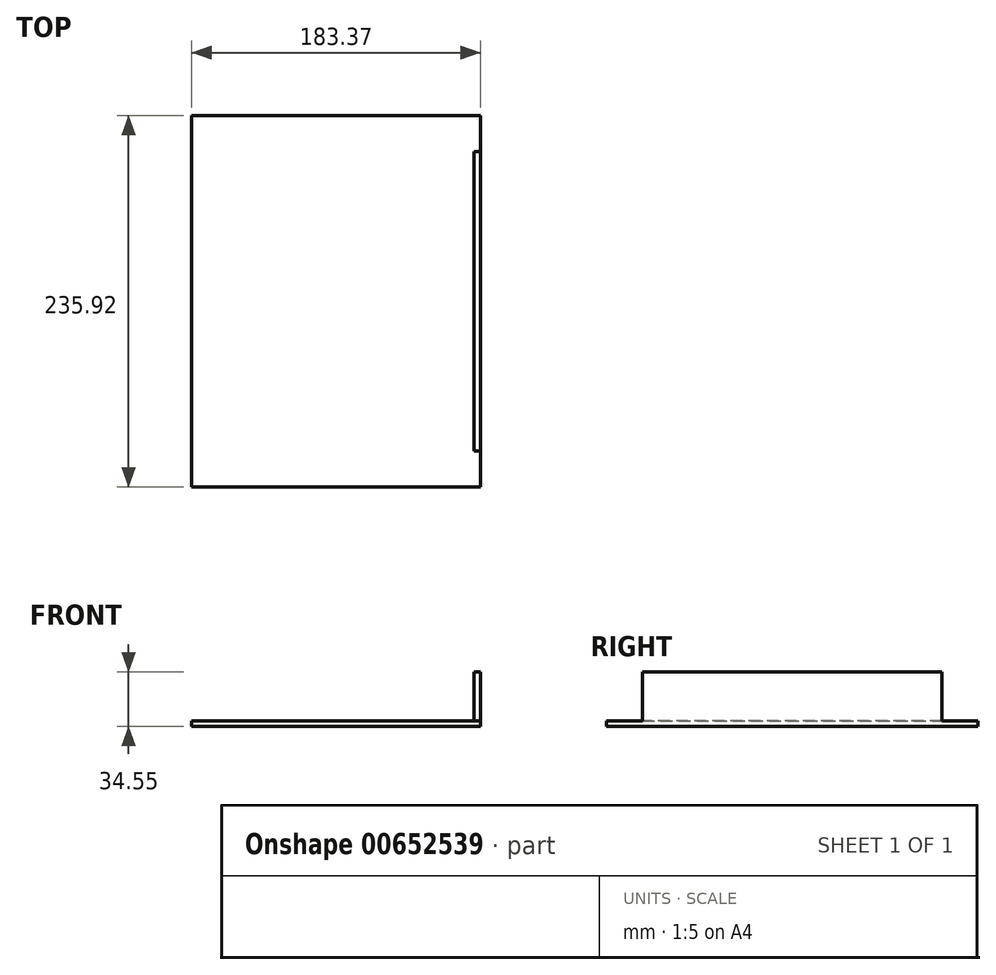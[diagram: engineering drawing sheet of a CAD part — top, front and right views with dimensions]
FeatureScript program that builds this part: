
annotation { "Feature Type Name" : "Feature", "Feature Type Description" : "" }
export const myFeature = defineFeature(function(context is Context, id is Id, definition is map)
    precondition{}
    {
        {
            var Q0;
            Q0=qCreatedBy(makeId("Top.planeOp"),FACE);
            var sketch = newSketch(context, id + "F0", { "sketchPlane" : qUnion([Q0])});
            skLineSegment(sketch, "E0.bottom", {"start": v(-86.94, 111.9) * mm, "end": v(96.43, 111.9) * mm});
            skLineSegment(sketch, "E0.top", {"start": v(-86.94, -124.02) * mm, "end": v(96.43, -124.02) * mm});
            skLineSegment(sketch, "E0.left", {"start": v(-86.94, 111.9) * mm, "end": v(-86.94, -124.02) * mm});
            skLineSegment(sketch, "E0.right", {"start": v(96.43, 111.9) * mm, "end": v(96.43, -124.02) * mm});
            skSolve(sketch);
        }
        {
            var Q0;
            Q0=makeQuery(id+"F0.imprint","IMPRINT",FACE,{"disambiguationData":[TD([[makeQuery(id+"F0.imprint","IMPRINT",EDGE,{"derivedFrom":sQuery(id+"F0.wireOp",EDGE,"E0.bottom")}),-1.0]])]});
            extrude(context, id + "F1", {"entities" : qUnion([Q0]), "oppositeDirection" : true, "depth" : 3.56 * mm, "offsetDistance" : 25.4 * mm});
        }
        {
            var Q0;
            Q0=makeQuery(id+"F1.opExtrude","CAP_FACE",FACE,{"disambiguationData":[OSD([sQuery(id+"F0.wireOp",EDGE,"E0.bottom"),sQuery(id+"F0.wireOp",EDGE,"E0.top"),sQuery(id+"F0.wireOp",EDGE,"E0.left"),sQuery(id+"F0.wireOp",EDGE,"E0.right")])],"isStart":true});
            var sketch = newSketch(context, id + "F2", { "sketchPlane" : qUnion([Q0])});
            skLineSegment(sketch, "E1.bottom", {"start": v(92.31, -101.03) * mm, "end": v(96.43, -101.03) * mm});
            skLineSegment(sketch, "E1.top", {"start": v(92.31, 89) * mm, "end": v(96.43, 89) * mm});
            skLineSegment(sketch, "E1.left", {"start": v(92.31, -101.03) * mm, "end": v(92.31, 89) * mm});
            skLineSegment(sketch, "E1.right", {"start": v(96.43, -101.03) * mm, "end": v(96.43, 89) * mm});
            skSolve(sketch);
        }
        {
            var Q0;
            Q0=makeQuery(id+"F2.imprint","IMPRINT",FACE,{"disambiguationData":[TD([[makeQuery(id+"F2.imprint","IMPRINT",EDGE,{"derivedFrom":sQuery(id+"F2.wireOp",EDGE,"E1.bottom")}),1.0]])]});
            extrude(context, id + "F3", {"entities" : qUnion([Q0]), "operationType" : NewBodyOperationType.ADD, "depth" : 30.99 * mm, "offsetDistance" : 25.4 * mm});
        }
    });
